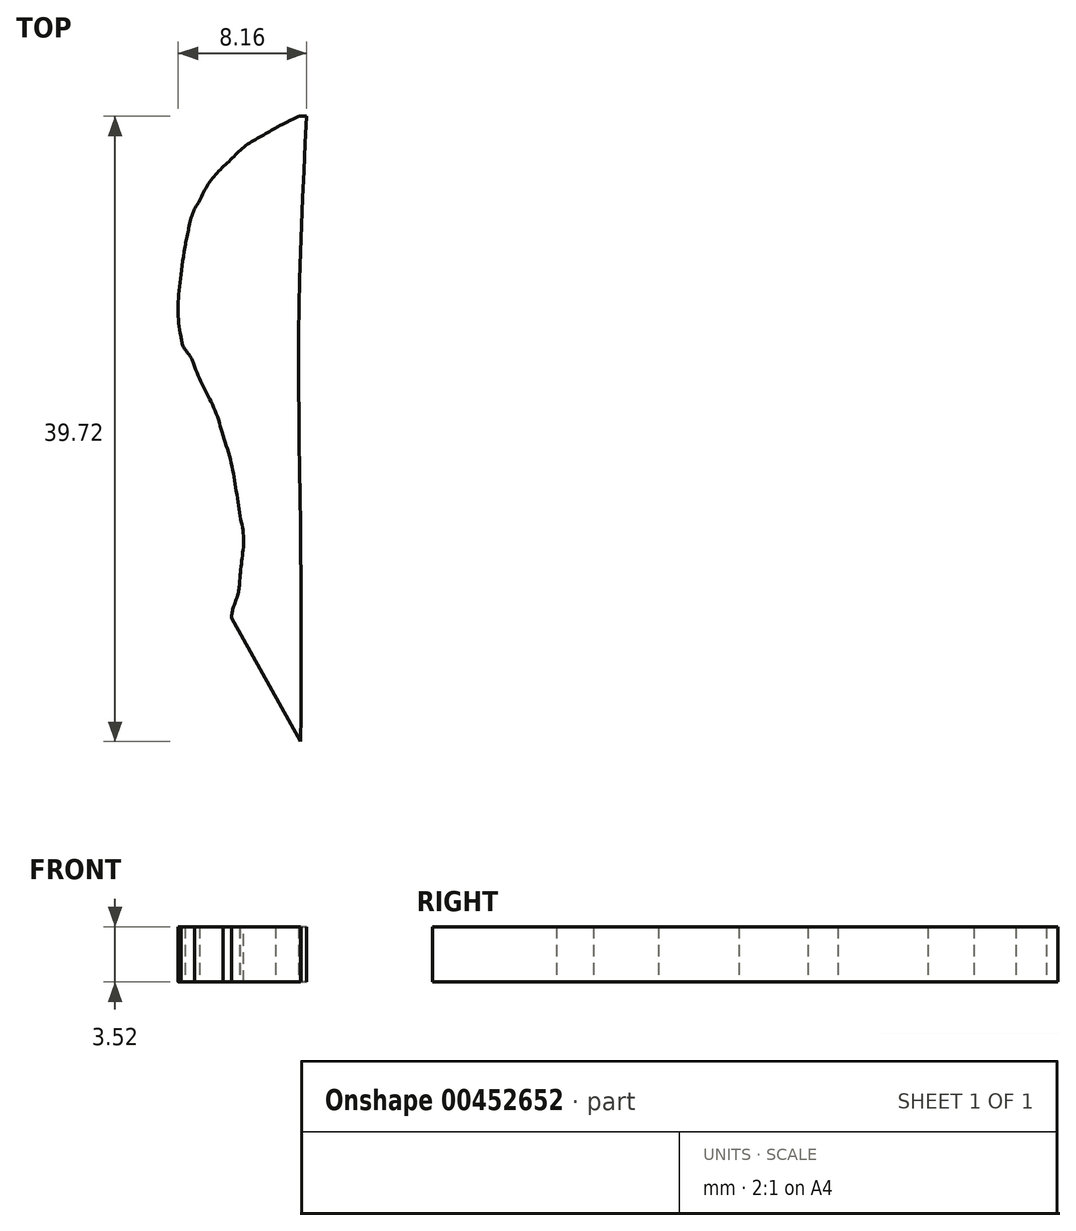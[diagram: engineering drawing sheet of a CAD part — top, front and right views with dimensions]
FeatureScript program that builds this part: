
annotation { "Feature Type Name" : "Feature", "Feature Type Description" : "" }
export const myFeature = defineFeature(function(context is Context, id is Id, definition is map)
    precondition{}
    {
        {
            var Q0;
            Q0=qCreatedBy(makeId("Top.planeOp"),FACE);
            var sketch = newSketch(context, id + "F0", { "sketchPlane" : qUnion([Q0])});
            skFitSpline(sketch, "E0", {"points": [v(-412.2, -7196.56) * mm, v(-356.8, -6861.27) * mm, v(-172.67, -6313.91) * mm, v(-121.91, -5861.25) * mm]});
            skFitSpline(sketch, "E1", {"points": [v(-121.91, -5861.25) * mm, v(-34.83, -5084.73) * mm, v(23.44, -4318.64) * mm, v(-100.14, -3517.19) * mm]});
            skFitSpline(sketch, "E2", {"points": [v(-100.14, -3517.19) * mm, v(-250.75, -2540.5) * mm, v(-430.95, -1554.82) * mm, v(-724.26, -607.07) * mm]});
            skFitSpline(sketch, "E3", {"points": [v(-724.26, -607.07) * mm, v(-990.14, 252.07) * mm, v(-1389.16, 1064.52) * mm, v(-1747.51, 1889.38) * mm]});
            skFitSpline(sketch, "E4", {"points": [v(-1747.51, 1889.38) * mm, v(-1904.5, 2250.75) * mm, v(-2139.1, 2582.84) * mm, v(-2241, 2963.44) * mm]});
            skFitSpline(sketch, "E5", {"points": [v(-2095.85, 6214.64) * mm, v(-1973.92, 6783.14) * mm, v(-1836.2, 7361.66) * mm, v(-1566.08, 7876.53) * mm]});
            skFitSpline(sketch, "E6", {"points": [v(-1566.08, 7876.53) * mm, v(-1266.43, 8447.67) * mm, v(-849.5, 8962.2) * mm, v(-383.17, 9407.78) * mm]});
            skFitSpline(sketch, "E7", {"points": [v(-383.17, 9407.78) * mm, v(76.33, 9846.85) * mm, v(629.32, 10181.37) * mm, v(1177.12, 10503.61) * mm]});
            skFitSpline(sketch, "E8", {"points": [v(2342.6, 11671.5) * mm, v(2025.5, 3887.3) * mm, v(2077.64, -3883.82) * mm, v(2090.87, -11671.5) * mm]});
            skLineSegment(sketch, "E9", {"start": v(2040.72, 10922.04) * mm, "end": v(2342.6, 11671.5) * mm});
            skLineSegment(sketch, "E10", {"start": v(2342.6, 11671.5) * mm, "end": v(2040.72, 10922.04) * mm});
            skFitSpline(sketch, "E11", {"points": [v(1177.12, 10503.61) * mm, v(2040.72, 10922.04) * mm], "startDerivative": vector(1228.85, 665.81) * mm, "endDerivative": vector(984.27, 443.85) * mm});
            skLineSegment(sketch, "E12", {"start": v(-412.2, -7196.56) * mm, "end": v(2090.87, -11671.5) * mm});
            skFitSpline(sketch, "E13", {"points": [v(-2241, 2963.44) * mm, v(-2095.85, 6214.64) * mm], "startDerivative": vector(-601.72, 2855.9) * mm, "endDerivative": vector(624.12, 4225.15) * mm});
            skSolve(sketch);
        }
        {
            var Q0;
            Q0=makeQuery(id+"F0.imprint","IMPRINT",FACE,{"disambiguationData":[TD([[makeQuery(id+"F0.imprint","IMPRINT",EDGE,{"derivedFrom":sQuery(id+"F0.wireOp",EDGE,"E0")}),-1.0]])]});
            var Q1;
            Q1 = qConstructionFilter(qBodyType(qCreatedBy(id + "F0" ,EDGE), BodyType.WIRE), ConstructionObject.NO);
            extrude(context, id + "F1", {"entities" : qUnion([Q0]), "surfaceEntities" : qUnion([Q1]), "depth" : 2000 * mm});
        }
        {
            var Q0;
            Q0=makeQuery(id+"F1.opExtrude","SWEPT_BODY",BODY,{"disambiguationData":[OSD([sQuery(id+"F0.wireOp",EDGE,"E0"),sQuery(id+"F0.wireOp",EDGE,"E1"),sQuery(id+"F0.wireOp",EDGE,"E2"),sQuery(id+"F0.wireOp",EDGE,"E3"),sQuery(id+"F0.wireOp",EDGE,"E4"),sQuery(id+"F0.wireOp",EDGE,"E5"),sQuery(id+"F0.wireOp",EDGE,"E6"),sQuery(id+"F0.wireOp",EDGE,"E7"),sQuery(id+"F0.wireOp",EDGE,"E8"),sQuery(id+"F0.wireOp",EDGE,"E10"),sQuery(id+"F0.wireOp",EDGE,"E11"),sQuery(id+"F0.wireOp",EDGE,"E12"),sQuery(id+"F0.wireOp",EDGE,"E13")])]});
            var Q1;
            Q1=qCreatedBy(makeId("Origin.pointOp"),VERTEX);
            transform(context, id + "F2", {"entities" : qUnion([Q0]), "transformType" : TransformType.SCALE_UNIFORMLY, "scale" : 0, "scalePoint" : qUnion([Q1]), "makeCopy" : false});
        }
        {
            var Q0;
            Q0=makeQuery(id+"F1.opExtrude","SWEPT_BODY",BODY,{"disambiguationData":[OSD([sQuery(id+"F0.wireOp",EDGE,"E0"),sQuery(id+"F0.wireOp",EDGE,"E1"),sQuery(id+"F0.wireOp",EDGE,"E2"),sQuery(id+"F0.wireOp",EDGE,"E3"),sQuery(id+"F0.wireOp",EDGE,"E4"),sQuery(id+"F0.wireOp",EDGE,"E5"),sQuery(id+"F0.wireOp",EDGE,"E6"),sQuery(id+"F0.wireOp",EDGE,"E7"),sQuery(id+"F0.wireOp",EDGE,"E8"),sQuery(id+"F0.wireOp",EDGE,"E10"),sQuery(id+"F0.wireOp",EDGE,"E11"),sQuery(id+"F0.wireOp",EDGE,"E12"),sQuery(id+"F0.wireOp",EDGE,"E13")])]});
            var Q1;
            Q1=qCreatedBy(makeId("Origin.pointOp"),VERTEX);
            transform(context, id + "F3", {"entities" : qUnion([Q0]), "transformType" : TransformType.SCALE_UNIFORMLY, "scale" : 0.88, "scalePoint" : qUnion([Q1]), "makeCopy" : false});
        }
        {
            var Q0;
            Q0=makeQuery(id+"F1.opExtrude","CAP_FACE",FACE,{"disambiguationData":[OSD([sQuery(id+"F0.wireOp",EDGE,"E0"),sQuery(id+"F0.wireOp",EDGE,"E1"),sQuery(id+"F0.wireOp",EDGE,"E2"),sQuery(id+"F0.wireOp",EDGE,"E3"),sQuery(id+"F0.wireOp",EDGE,"E4"),sQuery(id+"F0.wireOp",EDGE,"E5"),sQuery(id+"F0.wireOp",EDGE,"E6"),sQuery(id+"F0.wireOp",EDGE,"E7"),sQuery(id+"F0.wireOp",EDGE,"E8"),sQuery(id+"F0.wireOp",EDGE,"E10"),sQuery(id+"F0.wireOp",EDGE,"E11"),sQuery(id+"F0.wireOp",EDGE,"E12"),sQuery(id+"F0.wireOp",EDGE,"E13")])],"isStart":false});
            var sketch = newSketch(context, id + "F4", { "sketchPlane" : qUnion([Q0])});
            skLineSegment(sketch, "E14", {"start": v(4.12, 20.52) * mm, "end": v(3.68, -20.52) * mm});
            skSolve(sketch);
        }
        {
            var Q0;
            Q0=makeQuery(id+"F4.imprint","IMPRINT",FACE,{"disambiguationData":[TD([[makeQuery(id+"F4.imprint","IMPRINT",EDGE,{"derivedFrom":makeQuery(id+"F1.opExtrude","CAP_EDGE",EDGE,{"disambiguationData":[OSD([sQuery(id+"F0.wireOp",EDGE,"E0")])],"isStart":false})}),-1.0]])]});
            var sketch = newSketch(context, id + "F5", { "sketchPlane" : qUnion([Q0])});
            skLineSegment(sketch, "E15", {"start": v(3.59, 19.2) * mm, "end": v(4.46, 19.2) * mm});
            skLineSegment(sketch, "E16", {"start": v(3.59, 19.2) * mm, "end": v(3.55, 20.6) * mm});
            skLineSegment(sketch, "E17", {"start": v(3.55, 20.6) * mm, "end": v(4.5, 20.68) * mm});
            skLineSegment(sketch, "E18", {"start": v(4.5, 20.68) * mm, "end": v(4.46, 19.2) * mm});
            skSolve(sketch);
        }
        {
            var Q0;
            Q0 = qSketchRegion(id + "F5", true);
            extrude(context, id + "F6", {"entities" : qUnion([Q0]), "operationType" : NewBodyOperationType.REMOVE, "oppositeDirection" : true, "depth" : 25 * mm});
        }
    });
